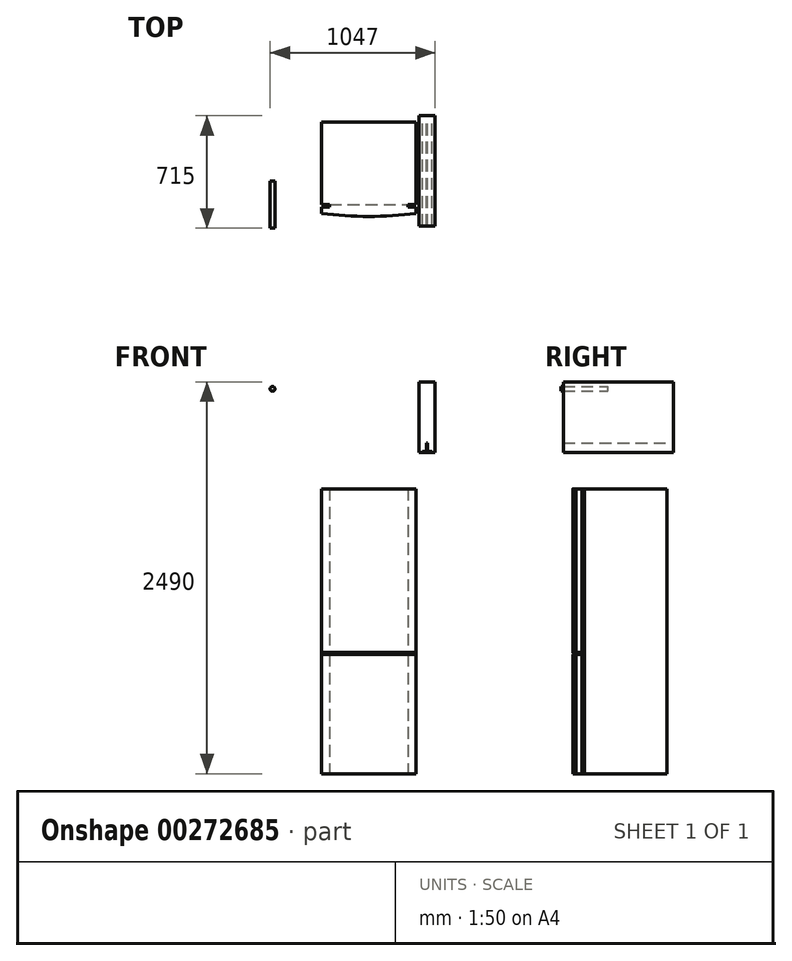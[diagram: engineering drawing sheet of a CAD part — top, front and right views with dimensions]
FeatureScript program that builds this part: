
annotation { "Feature Type Name" : "Feature", "Feature Type Description" : "" }
export const myFeature = defineFeature(function(context is Context, id is Id, definition is map)
    precondition{}
    {
        {
            var Q0;
            Q0=qCreatedBy(makeId("Front.planeOp"),FACE);
            var sketch = newSketch(context, id + "F0", { "sketchPlane" : qUnion([Q0])});
            skLineSegment(sketch, "E0.bottom", {"start": v(0, 0) * mm, "end": v(-990, 0) * mm});
            skLineSegment(sketch, "E0.top", {"start": v(0, 2540) * mm, "end": v(-995, 2540) * mm});
            skLineSegment(sketch, "E0.left", {"start": v(0, 0) * mm, "end": v(0, 2540) * mm});
            skLineSegment(sketch, "E0.right", {"start": v(-995, 750) * mm, "end": v(-995, 1860) * mm});
            skLineSegment(sketch, "E1", {"start": v(-995, 750) * mm, "end": v(-990, 0) * mm});
            skLineSegment(sketch, "E2.trimOffspring", {"start": v(-995, 1860) * mm, "end": v(-995, 2540) * mm});
            skSolve(sketch);
        }
        {
            var Q0;
            Q0=qCreatedBy(makeId("Front.planeOp"),FACE);
            cPlane(context, id + "F1", {"entities" : qUnion([Q0]), "cplaneType" : CPlaneType.OFFSET, "offset" : 640 * mm, "width" : 150 * mm, "height" : 150 * mm});
        }
        {
            var Q0;
            Q0=qCreatedBy(id+"F1.planeOp",FACE);
            var sketch = newSketch(context, id + "F2", { "sketchPlane" : qUnion([Q0])});
            skLineSegment(sketch, "E3.0", {"start": v(0, 2540) * mm, "end": v(-1005, 2540) * mm});
            skLineSegment(sketch, "E4.0", {"start": v(0, 0) * mm, "end": v(0, 2540) * mm});
            skLineSegment(sketch, "E5.0", {"start": v(0, 0) * mm, "end": v(-990, 0) * mm});
            skLineSegment(sketch, "E6", {"start": v(-990, 0) * mm, "end": v(-995, 750) * mm});
            skLineSegment(sketch, "E7", {"start": v(-995, 750) * mm, "end": v(-1005, 1860) * mm});
            skLineSegment(sketch, "E8", {"start": v(-1005, 1860) * mm, "end": v(-1005, 2540) * mm});
            skLineSegment(sketch, "E9", {"start": v(-995, 750) * mm, "end": v(-995, 750) * mm});
            skLineSegment(sketch, "E10", {"start": v(-1005, 1860) * mm, "end": v(-995, 1860) * mm, "construction": true});
            skSolve(sketch);
        }
        {
            var Q0;
            Q0=makeQuery(id+"F0.imprint","IMPRINT",FACE,{"disambiguationData":[TD([[makeQuery(id+"F0.imprint","IMPRINT",EDGE,{"derivedFrom":sQuery(id+"F0.wireOp",EDGE,"E0.bottom")}),-1.0]])]});
            var Q1;
            Q1 = qConstructionFilter(qBodyType(qCreatedBy(id + "F0" ,EDGE), BodyType.WIRE), ConstructionObject.NO);
            var Q2;
            Q2 = qConstructionFilter(qBodyType(qCreatedBy(id + "F2" ,EDGE), BodyType.WIRE), ConstructionObject.NO);
            loft(context, id + "F3", {"bodyType" : ToolBodyType.SURFACE, "sheetProfilesArray" : [{ "sheetProfileEntities" : qUnion([Q0]) }], "wireProfilesArray" : [{ "wireProfileEntities" : qUnion([Q1]) }, { "wireProfileEntities" : qUnion([Q2]) }]});
        }
        {
            var Q0;
            Q0=qCreatedBy(makeId("Front.planeOp"),FACE);
            var sketch = newSketch(context, id + "F4", { "sketchPlane" : qUnion([Q0])});
            skLineSegment(sketch, "E11.bottom", {"start": v(0, 2540) * mm, "end": v(100, 2540) * mm});
            skLineSegment(sketch, "E11.top", {"start": v(0, 2090) * mm, "end": v(100, 2090) * mm});
            skLineSegment(sketch, "E11.left", {"start": v(0, 2540) * mm, "end": v(0, 2090) * mm});
            skLineSegment(sketch, "E11.right", {"start": v(100, 2540) * mm, "end": v(100, 2090) * mm});
            skLineSegment(sketch, "E12", {"start": v(20, 2090) * mm, "end": v(20, 2098) * mm});
            skLineSegment(sketch, "E13", {"start": v(20, 2098) * mm, "end": v(46, 2098) * mm});
            skLineSegment(sketch, "E14", {"start": v(46, 2098) * mm, "end": v(46, 2150) * mm});
            skLineSegment(sketch, "E15", {"start": v(50, 2090) * mm, "end": v(50, 2150) * mm, "construction": true});
            skLineSegment(sketch, "E16.MirrorCS", {"start": v(54, 2098) * mm, "end": v(54, 2150) * mm});
            skLineSegment(sketch, "E17.MirrorCS", {"start": v(80, 2098) * mm, "end": v(54, 2098) * mm});
            skLineSegment(sketch, "E18.MirrorCS", {"start": v(80, 2090) * mm, "end": v(80, 2098) * mm});
            skLineSegment(sketch, "E19", {"start": v(46, 2150) * mm, "end": v(54, 2150) * mm});
            skSolve(sketch);
        }
        {
            var Q0;
            Q0=makeQuery(id+"F4.imprint","IMPRINT",FACE,{"disambiguationData":[TD([[makeQuery(id+"F4.imprint","IMPRINT",EDGE,{"derivedFrom":sQuery(id+"F4.wireOp",EDGE,"E11.bottom")}),-1.0]])]});
            var Q1;
            Q1=makeQuery(id+"F3.opLoft","MID_CAP_VERTEX",VERTEX,{"disambiguationData":[OSD([sQuery(id+"F2.wireOp",VERTEX,"E4.0.end")])],"capPos":1.0});
            extrude(context, id + "F5", {"entities" : qUnion([Q0]), "endBoundEntityVertex" : qUnion([Q1]), "depth" : 700 * mm});
        }
        {
            var Q0;
            {var subQ0=sQuery(id+"F4.wireOp",EDGE,"E12");Q0=makeQuery(id+"F4.imprint","IMPRINT",FACE,{"disambiguationData":[TD([[makeQuery(id+"F4.imprint","IMPRINT",EDGE,{"derivedFrom":subQ0}),-1.0]])]});}
            var Q1;
            Q1=makeQuery(id+"F5.opExtrude","CAP_VERTEX",VERTEX,{"disambiguationData":[OSD([sQuery(id+"F4.wireOp",EDGE,"E11.top"),sQuery(id+"F4.wireOp",EDGE,"E11.right")])],"isStart":false});
            extrude(context, id + "F6", {"entities" : qUnion([Q0]), "endBound" : BoundingType.UP_TO_VERTEX, "endBoundEntityVertex" : qUnion([Q1]), "depth" : 25 * mm});
        }
        {
            var Q0;
            Q0=qCreatedBy(makeId("Front.planeOp"),FACE);
            var sketch = newSketch(context, id + "F7", { "sketchPlane" : qUnion([Q0])});
            skCircle(sketch, "E20", {"center": v(-932, 2495) * mm, "radius": 15 * mm});
            skSolve(sketch);
        }
        {
            var Q0;
            Q0 = qSketchRegion(id + "F7", true);
            extrude(context, id + "F8", {"entities" : qUnion([Q0]), "depth" : 300 * mm});
        }
        {
            var Q0;
            Q0=makeQuery(id+"F8.opExtrude","SWEPT_BODY",BODY,{"disambiguationData":[OSD([sQuery(id+"F7.wireOp",EDGE,"E20")])]});
            transform(context, id + "F9", {"entities" : qUnion([Q0]), "transformType" : TransformType.TRANSLATION_3D, "dx" : 0 * mm, "dy" : -415 * mm, "dz" : 0 * mm, "makeCopy" : false});
        }
        {
            var Q0;
            Q0=qCreatedBy(makeId("Top.planeOp"),FACE);
            cPlane(context, id + "F10", {"entities" : qUnion([Q0]), "cplaneType" : CPlaneType.OFFSET, "offset" : 50 * mm, "width" : 150 * mm, "height" : 150 * mm});
        }
        {
            var Q0;
            Q0=qCreatedBy(id+"F10.planeOp",FACE);
            var sketch = newSketch(context, id + "F11", { "sketchPlane" : qUnion([Q0])});
            skLineSegment(sketch, "E21", {"start": v(-20, -40) * mm, "end": v(-20, -620) * mm});
            skLineSegment(sketch, "E22", {"start": v(-20, -620) * mm, "end": v(-620, -620) * mm, "construction": true});
            skLineSegment(sketch, "E23", {"start": v(-620, -620) * mm, "end": v(-620, -40) * mm});
            skLineSegment(sketch, "E24", {"start": v(-620, -40) * mm, "end": v(-20, -40) * mm});
            skArc(sketch, "E25", {"start": v(-620, -620) * mm, "mid": v(-320, -640) * mm, "end": v(-20, -620) * mm});
            skLineSegment(sketch, "E26", {"start": v(-620, -580) * mm, "end": v(-570, -580) * mm});
            skLineSegment(sketch, "E27", {"start": v(-570, -565) * mm, "end": v(-570, -580) * mm});
            skLineSegment(sketch, "E28", {"start": v(-570, -565) * mm, "end": v(-620, -565) * mm});
            skLineSegment(sketch, "E29", {"start": v(-320, -40) * mm, "end": v(-320, -620) * mm, "construction": true});
            skLineSegment(sketch, "E30.MirrorCS", {"start": v(-20, -580) * mm, "end": v(-70, -580) * mm});
            skLineSegment(sketch, "E31.MirrorCS", {"start": v(-70, -565) * mm, "end": v(-20, -565) * mm});
            skLineSegment(sketch, "E32.MirrorCS", {"start": v(-70, -565) * mm, "end": v(-70, -580) * mm});
            skSolve(sketch);
        }
        {
            var Q0;
            {var subQ2=sQuery(id+"F11.wireOp",EDGE,"E24");Q0=makeQuery(id+"F11.imprint","IMPRINT",FACE,{"disambiguationData":[TD([[makeQuery(id+"F11.imprint","IMPRINT",EDGE,{"derivedFrom":subQ2}),-1.0]])]});}
            extrude(context, id + "F12", {"entities" : qUnion([Q0]), "depth" : 1810 * mm});
        }
        {
            var Q0;
            Q0=makeQuery(id+"F12.opExtrude","SWEPT_FACE",FACE,{"disambiguationData":[OSD([sQuery(id+"F11.wireOp",EDGE,"E21")])]});
            var sketch = newSketch(context, id + "F13", { "sketchPlane" : qUnion([Q0])});
            skLineSegment(sketch, "E33.bottom", {"start": v(-640, 820) * mm, "end": v(-565, 820) * mm});
            skLineSegment(sketch, "E33.top", {"start": v(-640, 807) * mm, "end": v(-565, 807) * mm});
            skLineSegment(sketch, "E33.left", {"start": v(-640, 820) * mm, "end": v(-640, 807) * mm});
            skLineSegment(sketch, "E33.right", {"start": v(-565, 820) * mm, "end": v(-565, 807) * mm});
            skLineSegment(sketch, "E34", {"start": v(-640, 50) * mm, "end": v(-640, 1860) * mm, "construction": true});
            skSolve(sketch);
        }
        {
            var Q0;
            Q0 = qSketchRegion(id + "F13", true);
            var Q1;
            Q1=makeQuery(id+"F12.opExtrude","SWEPT_FACE",FACE,{"disambiguationData":[OSD([sQuery(id+"F11.wireOp",EDGE,"E23")])]});
            extrude(context, id + "F14", {"entities" : qUnion([Q0]), "operationType" : NewBodyOperationType.REMOVE, "endBound" : BoundingType.UP_TO_SURFACE, "oppositeDirection" : true, "endBoundEntityFace" : qUnion([Q1]), "depth" : 25 * mm});
        }
        {
            var Q0;
            Q0=makeQuery(id+"F3.opLoft","SWEPT_FACE",FACE,{"disambiguationData":[OSD([sQuery(id+"F0.wireOp",VERTEX,"E0.left.end"),sQuery(id+"F0.wireOp",VERTEX,"E2.trimOffspring.end"),sQuery(id+"F0.wireOp",EDGE,"E0.top"),sQuery(id+"F2.wireOp",VERTEX,"E4.0.end"),sQuery(id+"F2.wireOp",VERTEX,"E8.end"),sQuery(id+"F2.wireOp",EDGE,"E3.0")])]});
            var sketch = newSketch(context, id + "F15", { "sketchPlane" : qUnion([Q0])});
            skFitSpline(sketch, "E35", {"points": [v(-984.26, -582.23) * mm, v(-835.53, -563.16) * mm, v(-662.02, -582.23) * mm, v(-471.34, -565.06) * mm, v(-263.5, -587.95) * mm, v(-116.7, -570.78) * mm, v(-8.3, -593.15) * mm], "startDerivative": vector(927.03, 197.06) * mm, "endDerivative": vector(837.1, -302.31) * mm});
            skSolve(sketch);
        }
        {
            var Q0;
            Q0=sQuery(id+"F15.wireOp",EDGE,"E35");
            extrude(context, id + "F16", {"bodyType" : ToolBodyType.SURFACE, "surfaceEntities" : qUnion([Q0]), "oppositeDirection" : true, "depth" : 400 * mm, "offsetDistance" : 25 * mm});
        }
    });
